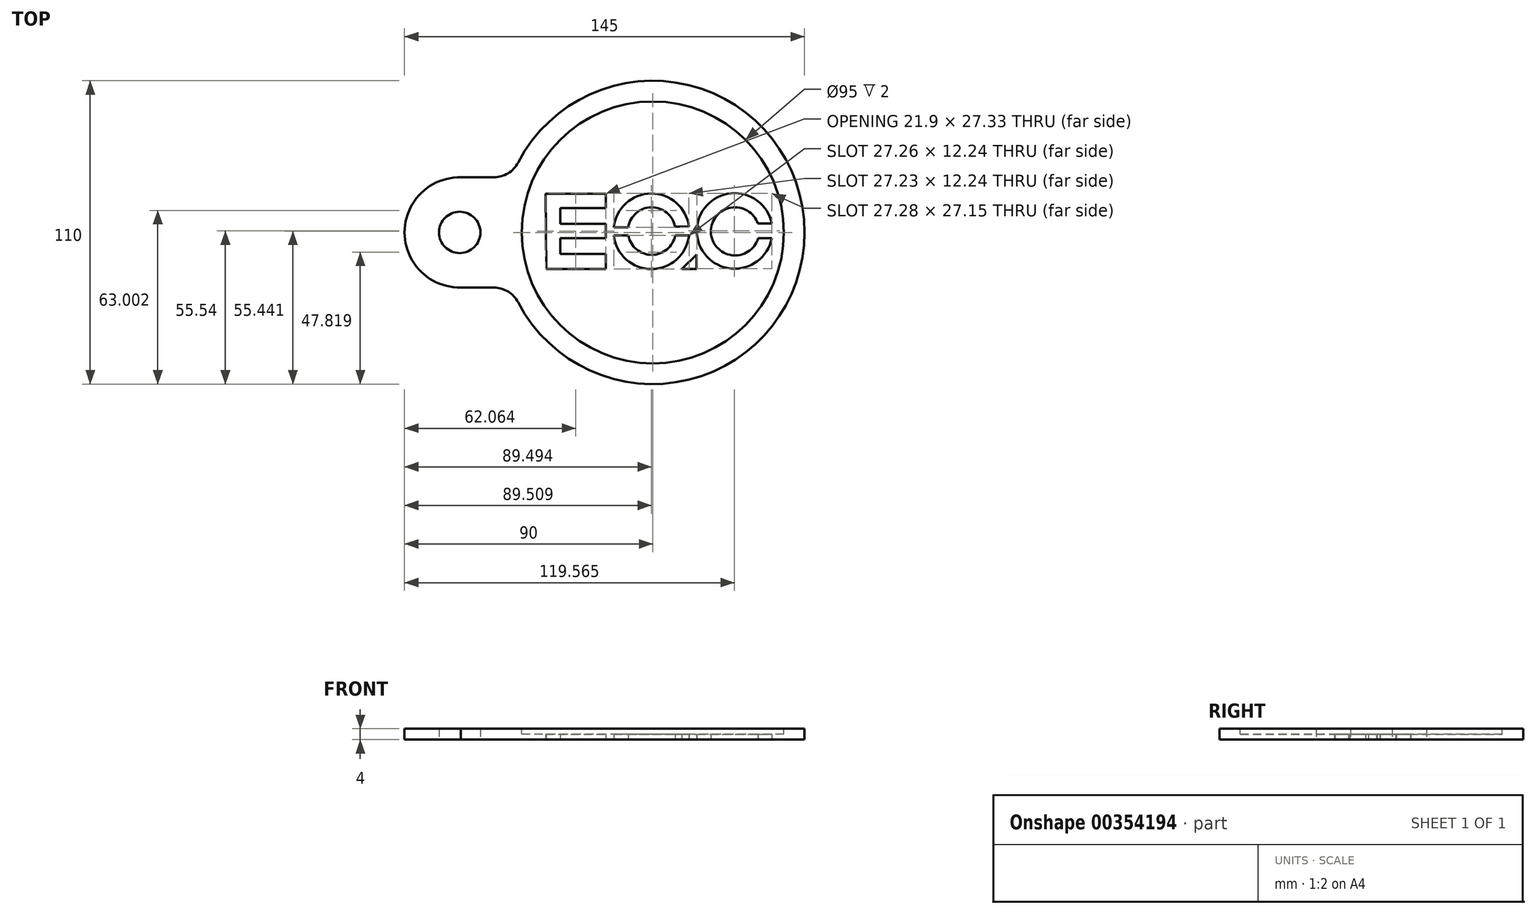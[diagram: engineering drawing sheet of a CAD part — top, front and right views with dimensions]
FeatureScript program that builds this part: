
annotation { "Feature Type Name" : "Feature", "Feature Type Description" : "" }
export const myFeature = defineFeature(function(context is Context, id is Id, definition is map)
    precondition{}
    {
        {
            var Q0;
            Q0=qCreatedBy(makeId("Top.planeOp"),FACE);
            var sketch = newSketch(context, id + "F0", { "sketchPlane" : qUnion([Q0])});
            skArc(sketch, "E0", {"start": v(48.8, 25.38) * mm, "mid": v(0, 55) * mm, "end": v(-48.8, 25.38) * mm});
            skPoint(sketch, "E1.visualSharp", {"position": v(51.24, 20) * mm});
            skPoint(sketch, "E2.visualSharp", {"position": v(51.24, -20) * mm});
            skArc(sketch, "E3.MirrorCS", {"start": v(-69.58, -20) * mm, "mid": v(-90, 0) * mm, "end": v(-69.58, 20) * mm});
            skCircle(sketch, "E4.MirrorC", {"center": v(-70, 0) * mm, "radius": 7.5 * mm});
            skArc(sketch, "E5.MirrorCS", {"start": v(-57.67, -20) * mm, "mid": v(-52.48, -21.45) * mm, "end": v(-48.8, -25.38) * mm});
            skLineSegment(sketch, "E6.MirrorCS", {"start": v(-69.58, 20) * mm, "end": v(-57.67, 20) * mm});
            skLineSegment(sketch, "E7.MirrorCS", {"start": v(-69.58, -20) * mm, "end": v(-57.67, -20) * mm});
            skArc(sketch, "E8.MirrorCS", {"start": v(-48.8, 25.38) * mm, "mid": v(-52.48, 21.45) * mm, "end": v(-57.67, 20) * mm});
            skArc(sketch, "E9.MirrorCS", {"start": v(-48.8, 25.38) * mm, "mid": v(55, 0) * mm, "end": v(-48.8, -25.38) * mm});
            skArc(sketch, "E10.trimOffspring", {"start": v(-48.8, -25.38) * mm, "mid": v(0, -55) * mm, "end": v(48.8, -25.38) * mm});
            skLineSegment(sketch, "E11", {"start": v(-38.89, 14.1) * mm, "end": v(-16.99, 14.1) * mm});
            skLineSegment(sketch, "E12", {"start": v(-16.99, 14.1) * mm, "end": v(-16.99, 8.78) * mm});
            skLineSegment(sketch, "E13", {"start": v(-16.99, 8.78) * mm, "end": v(-33.57, 8.78) * mm});
            skLineSegment(sketch, "E14", {"start": v(-33.57, 8.78) * mm, "end": v(-33.57, 3.15) * mm});
            skLineSegment(sketch, "E15", {"start": v(-33.57, 3.15) * mm, "end": v(-16.99, 3.15) * mm});
            skLineSegment(sketch, "E16", {"start": v(-16.99, 3.15) * mm, "end": v(-16.99, -2.07) * mm});
            skLineSegment(sketch, "E17", {"start": v(-16.99, -2.07) * mm, "end": v(-33.57, -2.07) * mm});
            skLineSegment(sketch, "E18", {"start": v(-33.57, -2.07) * mm, "end": v(-33.57, -7.8) * mm});
            skLineSegment(sketch, "E19", {"start": v(-33.57, -7.8) * mm, "end": v(-16.99, -7.8) * mm});
            skLineSegment(sketch, "E20", {"start": v(-16.99, -7.8) * mm, "end": v(-16.99, -13.22) * mm});
            skLineSegment(sketch, "E21", {"start": v(-16.99, -13.22) * mm, "end": v(-38.68, -13.22) * mm});
            skLineSegment(sketch, "E22", {"start": v(-38.68, -13.22) * mm, "end": v(-38.89, 14.1) * mm});
            skArc(sketch, "E23", {"start": v(-8.86, -1.06) * mm, "mid": v(-0.38, -8.14) * mm, "end": v(8.1, -1.06) * mm});
            skPoint(sketch, "E23.first.point", {"position": v(-4.3, 8.17) * mm});
            skPoint(sketch, "E23.second.point", {"position": v(8.09, 2.13) * mm});
            skPoint(sketch, "E23.third.point", {"position": v(-4.7, -6.98) * mm});
            skArc(sketch, "E24", {"start": v(-14.12, -1.06) * mm, "mid": v(-0.5, -13.3) * mm, "end": v(13.14, -1.06) * mm});
            skPoint(sketch, "E24.first.point", {"position": v(-5.73, 13.08) * mm});
            skPoint(sketch, "E24.second.point", {"position": v(13.2, 1) * mm});
            skPoint(sketch, "E24.third.point", {"position": v(-6.54, -11.9) * mm});
            skArc(sketch, "E25", {"start": v(38.08, 3.18) * mm, "mid": v(21.07, 0.22) * mm, "end": v(38.18, -2.1) * mm});
            skPoint(sketch, "E25.first.point", {"position": v(25.28, 7.86) * mm});
            skPoint(sketch, "E25.second.point", {"position": v(37.46, -3.81) * mm});
            skPoint(sketch, "E25.third.point", {"position": v(25.28, -7.09) * mm});
            skArc(sketch, "E26", {"start": v(43.14, 3.18) * mm, "mid": v(15.99, 0.54) * mm, "end": v(43.14, -2.1) * mm});
            skPoint(sketch, "E26.first.point", {"position": v(21.8, 11.74) * mm});
            skPoint(sketch, "E26.second.point", {"position": v(42.07, 6.43) * mm});
            skPoint(sketch, "E26.third.point", {"position": v(27.75, -13.02) * mm});
            skLineSegment(sketch, "E27", {"start": v(38.08, 3.18) * mm, "end": v(43.14, 3.18) * mm});
            skLineSegment(sketch, "E28", {"start": v(38.18, -2.1) * mm, "end": v(43.14, -2.1) * mm});
            skLineSegment(sketch, "E29", {"start": v(-14.12, 1.88) * mm, "end": v(-8.89, 1.88) * mm});
            skLineSegment(sketch, "E30", {"start": v(-14.12, -1.06) * mm, "end": v(-8.86, -1.06) * mm});
            skLineSegment(sketch, "E31", {"start": v(8.09, 2.13) * mm, "end": v(13.11, 2.13) * mm});
            skLineSegment(sketch, "E32", {"start": v(8.1, -1.06) * mm, "end": v(13.14, -1.06) * mm});
            skArc(sketch, "E33.trimOffspring", {"start": v(8.09, 2.13) * mm, "mid": v(-0.5, 9.1) * mm, "end": v(-8.89, 1.88) * mm});
            skArc(sketch, "E34.trimOffspring", {"start": v(13.11, 2.13) * mm, "mid": v(-0.62, 14.12) * mm, "end": v(-14.12, 1.88) * mm});
            skPoint(sketch, "E35", {"position": v(-38.78, 0.44) * mm});
            skLineSegment(sketch, "E36", {"start": v(-38.78, 0.44) * mm, "end": v(50.11, 0.44) * mm, "construction": true});
            skLineSegment(sketch, "E37.MirrorCS", {"start": v(10.55, -13.32) * mm, "end": v(15.87, -13.32) * mm});
            skLineSegment(sketch, "E38.MirrorCS", {"start": v(15.87, -8.1) * mm, "end": v(10.55, -13.32) * mm});
            skLineSegment(sketch, "E39.MirrorCS", {"start": v(15.87, -13.32) * mm, "end": v(15.87, -8.1) * mm});
            skSolve(sketch);
        }
        {
            var Q0;
            Q0=qSketchRegion(id+"F0",true);
            extrude(context, id + "F1", {"entities" : qUnion([Q0]), "depth" : 4 * mm});
        }
        {
            var Q0;
            Q0=makeQuery(id+"F1.opExtrude","CAP_FACE",FACE,{"disambiguationData":[OSD([sQuery(id+"F0.wireOp",EDGE,"E4.MirrorC"),sQuery(id+"F0.wireOp",EDGE,"E5.MirrorCS"),sQuery(id+"F0.wireOp",EDGE,"E7.MirrorCS"),sQuery(id+"F0.wireOp",EDGE,"E8.MirrorCS"),sQuery(id+"F0.wireOp",EDGE,"E9.MirrorCS"),sQuery(id+"F0.wireOp",EDGE,"E6.MirrorCS"),sQuery(id+"F0.wireOp",EDGE,"E3.MirrorCS"),sQuery(id+"F0.wireOp",EDGE,"E10.trimOffspring"),sQuery(id+"F0.wireOp",EDGE,"E11"),sQuery(id+"F0.wireOp",EDGE,"E12"),sQuery(id+"F0.wireOp",EDGE,"E13"),sQuery(id+"F0.wireOp",EDGE,"E14"),sQuery(id+"F0.wireOp",EDGE,"E15"),sQuery(id+"F0.wireOp",EDGE,"E16"),sQuery(id+"F0.wireOp",EDGE,"E17"),sQuery(id+"F0.wireOp",EDGE,"E18"),sQuery(id+"F0.wireOp",EDGE,"E19"),sQuery(id+"F0.wireOp",EDGE,"E20"),sQuery(id+"F0.wireOp",EDGE,"E21"),sQuery(id+"F0.wireOp",EDGE,"E22"),sQuery(id+"F0.wireOp",EDGE,"E23"),sQuery(id+"F0.wireOp",EDGE,"E24"),sQuery(id+"F0.wireOp",EDGE,"E25"),sQuery(id+"F0.wireOp",EDGE,"E26"),sQuery(id+"F0.wireOp",EDGE,"E27"),sQuery(id+"F0.wireOp",EDGE,"E28"),sQuery(id+"F0.wireOp",EDGE,"E29"),sQuery(id+"F0.wireOp",EDGE,"E30"),sQuery(id+"F0.wireOp",EDGE,"E31"),sQuery(id+"F0.wireOp",EDGE,"E32"),sQuery(id+"F0.wireOp",EDGE,"E33.trimOffspring"),sQuery(id+"F0.wireOp",EDGE,"E34.trimOffspring"),sQuery(id+"F0.wireOp",EDGE,"E37.MirrorCS"),sQuery(id+"F0.wireOp",EDGE,"E38.MirrorCS"),sQuery(id+"F0.wireOp",EDGE,"E39.MirrorCS")])],"isStart":false});
            var sketch = newSketch(context, id + "F2", { "sketchPlane" : qUnion([Q0])});
            skCircle(sketch, "E40", {"center": v(0, 0) * mm, "radius": 47.5 * mm});
            skSolve(sketch);
        }
        {
            var Q0;
            Q0=makeQuery(id+"F2.imprint","IMPRINT",FACE,{"disambiguationData":[TD([[makeQuery(id+"F2.imprint","IMPRINT",EDGE,{"derivedFrom":sQuery(id+"F2.wireOp",EDGE,"E40")}),1.0]])]});
            extrude(context, id + "F3", {"entities" : qUnion([Q0]), "operationType" : NewBodyOperationType.REMOVE, "oppositeDirection" : true, "depth" : 2 * mm});
        }
    });
